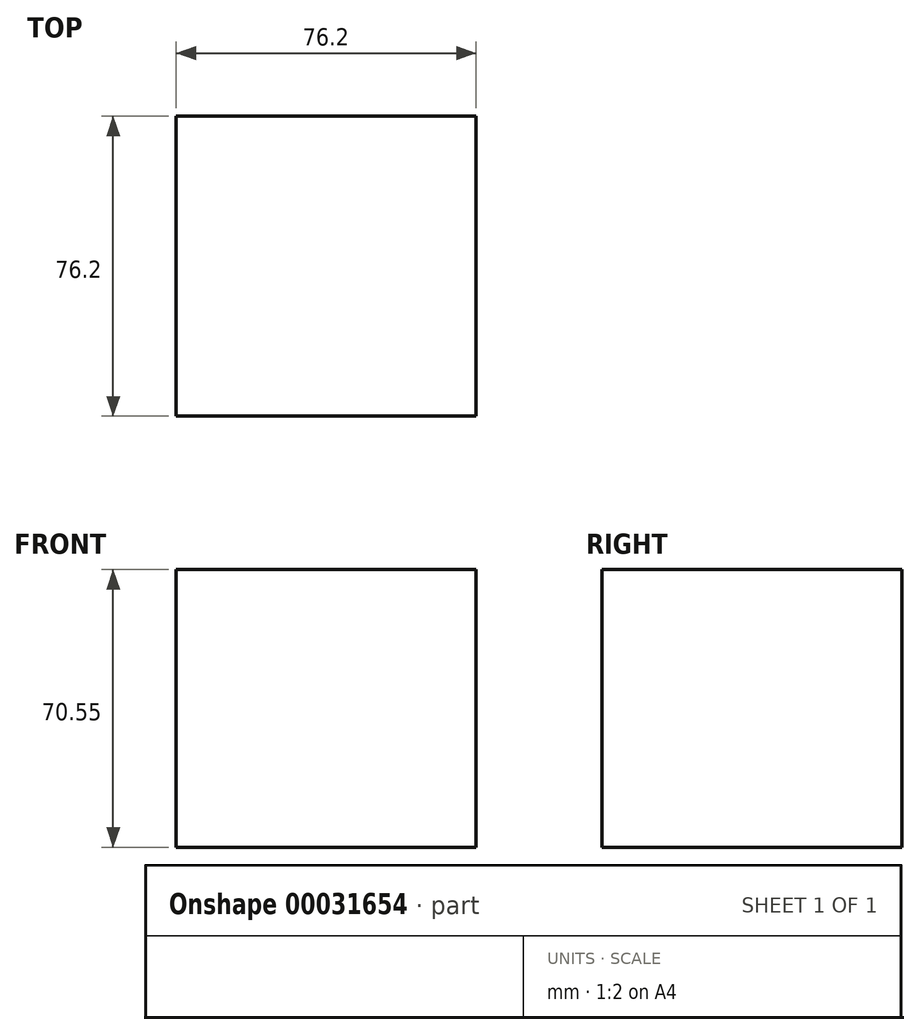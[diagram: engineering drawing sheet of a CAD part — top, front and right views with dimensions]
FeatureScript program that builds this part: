
annotation { "Feature Type Name" : "Feature", "Feature Type Description" : "" }
export const myFeature = defineFeature(function(context is Context, id is Id, definition is map)
    precondition{}
    {
        {
            var Q0;
            Q0=qCreatedBy(makeId("Front.planeOp"),FACE);
            var sketch = newSketch(context, id + "F0", { "sketchPlane" : qUnion([Q0])});
            skLineSegment(sketch, "E0.bottom", {"start": v(-32.36, 32.98) * mm, "end": v(43.84, 32.98) * mm});
            skLineSegment(sketch, "E0.top", {"start": v(-32.36, -37.57) * mm, "end": v(43.84, -37.57) * mm});
            skLineSegment(sketch, "E0.left", {"start": v(-32.36, 32.98) * mm, "end": v(-32.36, -37.57) * mm});
            skLineSegment(sketch, "E0.right", {"start": v(43.84, 32.98) * mm, "end": v(43.84, -37.57) * mm});
            skSolve(sketch);
        }
        {
            var Q0;
            Q0=makeQuery(id+"F0.imprint","IMPRINT",FACE,{"disambiguationData":[TD([[makeQuery(id+"F0.imprint","IMPRINT",EDGE,{"derivedFrom":sQuery(id+"F0.wireOp",EDGE,"E0.bottom")}),-1.0]])]});
            extrude(context, id + "F2", {"entities" : qUnion([Q0]), "depth" : 76.2 * mm});
        }
    });
